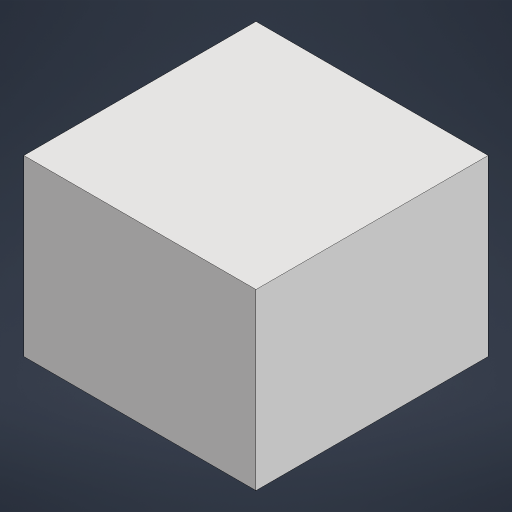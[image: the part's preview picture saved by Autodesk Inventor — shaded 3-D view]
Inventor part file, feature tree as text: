
AUTODESK INVENTOR PART (.ipt)
format: ipt  version: 2023.1 (Build 271208000, 208)  size: 122,368 bytes
history: native  units: in
note: dims shown in document units (in); Inventor stores cm internally (conversion verified against a paired STEP export)
features: extrude x1, sketch x1
ambient origin geometry x8: Origin, YZ Plane, XZ Plane, XY Plane, X Axis, Y Axis, Z Axis, Center Point
bodies: Solid1 (feature_tree)
feature tree (2):
  extrude  "Extrusion1"  Depth=4.0in
  sketch  "Sketch2"  dims[d3=4.0in d4=4.0in d5=3.0in d6=0.0in]
